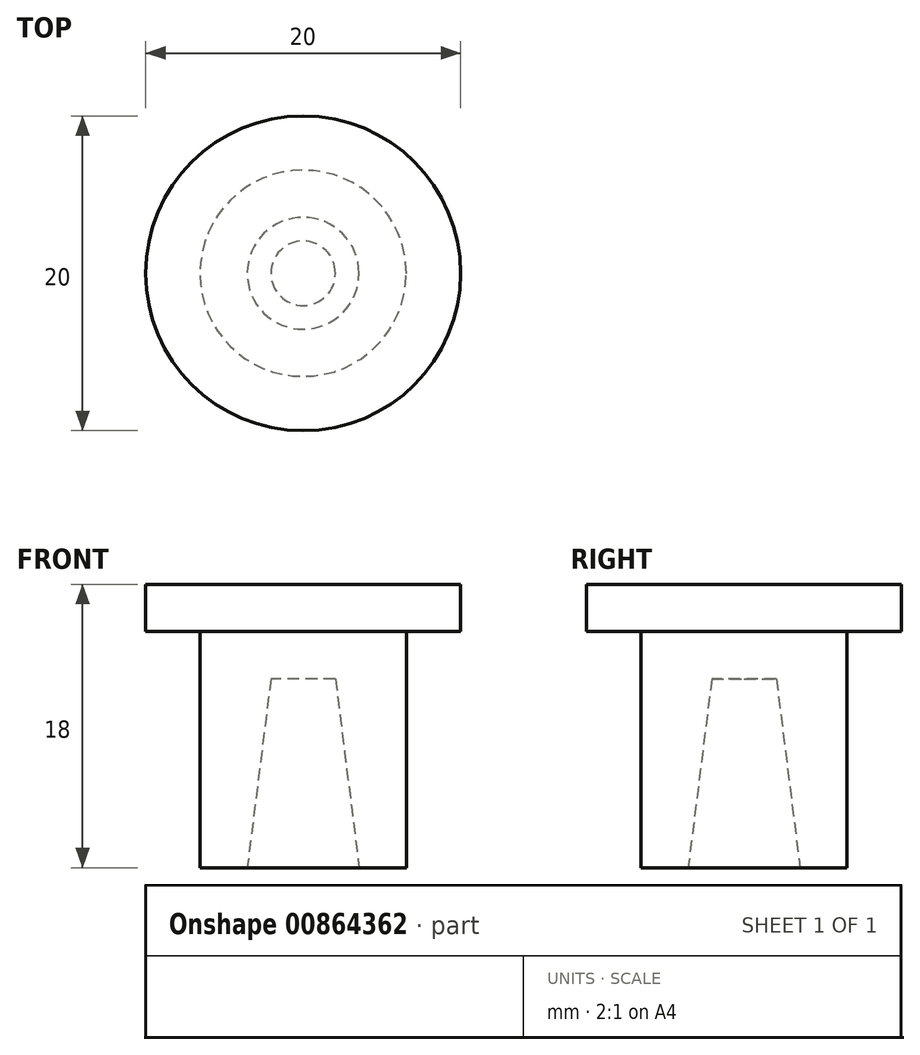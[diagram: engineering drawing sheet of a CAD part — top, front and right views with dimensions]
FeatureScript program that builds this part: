
annotation { "Feature Type Name" : "Feature", "Feature Type Description" : "" }
export const myFeature = defineFeature(function(context is Context, id is Id, definition is map)
    precondition{}
    {
        {
            var Q0;
            Q0=qCreatedBy(makeId("Front.planeOp"),FACE);
            var sketch = newSketch(context, id + "F0", { "sketchPlane" : qUnion([Q0])});
            skLineSegment(sketch, "E0", {"start": v(0, 18.18) * mm, "end": v(0, -10.4) * mm, "construction": true});
            skLineSegment(sketch, "E1", {"start": v(3.55, 0) * mm, "end": v(2.05, 12) * mm});
            skLineSegment(sketch, "E2", {"start": v(2.05, 12) * mm, "end": v(0, 12) * mm});
            skLineSegment(sketch, "E3.0", {"start": v(6.55, 15) * mm, "end": v(0, 15) * mm});
            skLineSegment(sketch, "E4", {"start": v(3.55, 0) * mm, "end": v(6.55, 0) * mm});
            skPoint(sketch, "E5.orphan", {"position": v(0, 11.99) * mm});
            skLineSegment(sketch, "E6", {"start": v(0, 15) * mm, "end": v(0, 12) * mm});
            skLineSegment(sketch, "E7", {"start": v(6.55, 0) * mm, "end": v(6.55, 15) * mm});
            skPoint(sketch, "E8.orphan", {"position": v(5, 15) * mm});
            skSolve(sketch);
        }
        {
            var Q0;
            Q0=makeQuery(id+"F0.imprint","IMPRINT",FACE,{"disambiguationData":[TD([[makeQuery(id+"F0.imprint","IMPRINT",EDGE,{"derivedFrom":sQuery(id+"F0.wireOp",EDGE,"E1")}),-1.0]])]});
            var Q1;
            Q1=sQuery(id+"F0.wireOp",EDGE,"E0");
            revolve(context, id + "F1", {"surfaceOperationType" : NewSurfaceOperationType.NEW, "entities" : qUnion([Q0]), "axis" : qUnion([Q1]), "revolveType" : RevolveType.FULL});
        }
        {
            var Q0;
            Q0=makeQuery(id+"F1.opRevolve","SWEPT_FACE",FACE,{"disambiguationData":[OSD([sQuery(id+"F0.wireOp",EDGE,"E3.0")])]});
            var sketch = newSketch(context, id + "F2", { "sketchPlane" : qUnion([Q0])});
            skCircle(sketch, "E9", {"center": v(0, 0) * mm, "radius": 10 * mm});
            skSolve(sketch);
        }
        {
            var Q0;
            Q0 = qSketchRegion(id + "F2", true);
            extrude(context, id + "F3", {"entities" : qUnion([Q0]), "operationType" : NewBodyOperationType.ADD, "depth" : 3 * mm, "offsetDistance" : 25 * mm});
        }
    });
